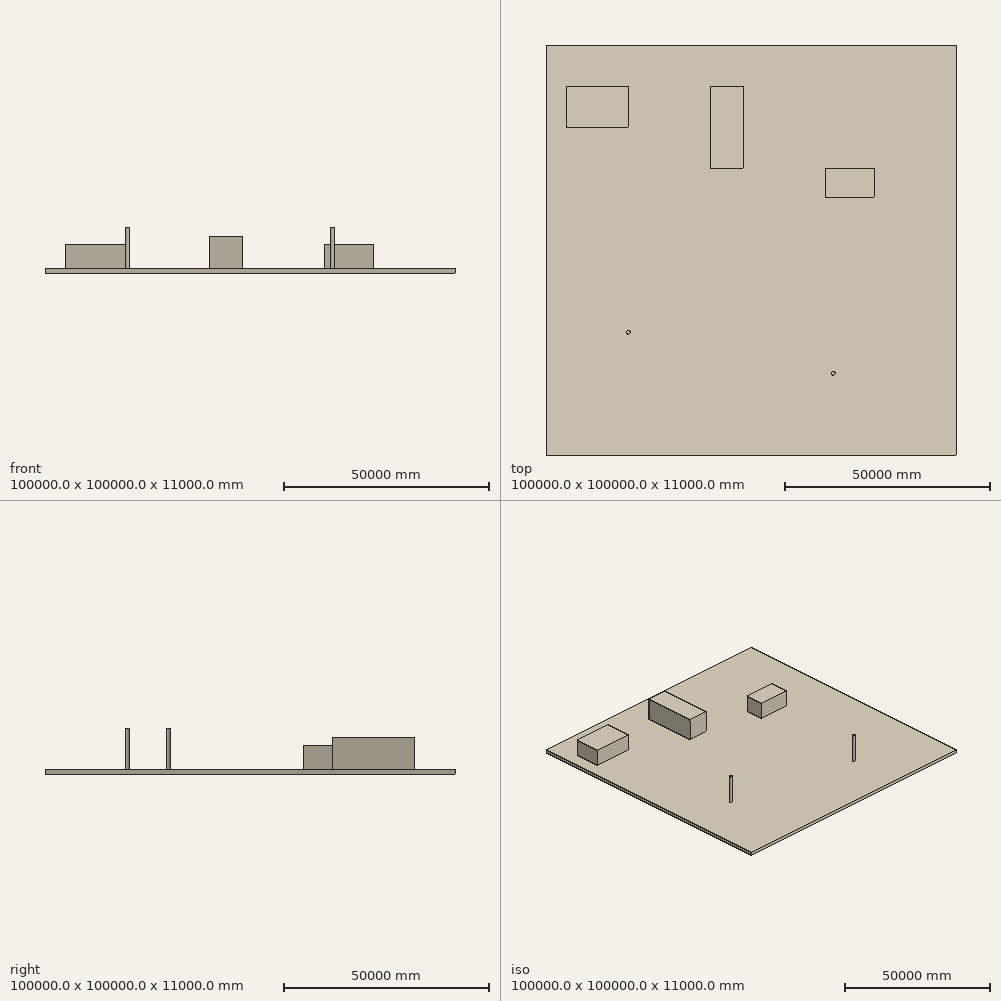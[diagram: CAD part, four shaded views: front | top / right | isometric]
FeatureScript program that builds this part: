
annotation { "Feature Type Name" : "Feature", "Feature Type Description" : "" }
export const myFeature = defineFeature(function(context is Context, id is Id, definition is map)
    precondition{}
    {
        {
            var Q0;
            Q0=qCreatedBy(makeId("Top.planeOp"),FACE);
            var sketch = newSketch(context, id + "F0", { "sketchPlane" : qUnion([Q0])});
            skLineSegment(sketch, "E0.bottom", {"start": v(-50000, 50000) * mm, "end": v(50000, 50000) * mm});
            skLineSegment(sketch, "E0.top", {"start": v(-50000, -50000) * mm, "end": v(50000, -50000) * mm});
            skLineSegment(sketch, "E0.left", {"start": v(-50000, 50000) * mm, "end": v(-50000, -50000) * mm});
            skLineSegment(sketch, "E0.right", {"start": v(50000, 50000) * mm, "end": v(50000, -50000) * mm});
            skPoint(sketch, "E0.middle", {"position": v(0, 0) * mm});
            skSolve(sketch);
        }
        {
            var Q0;
            Q0=makeQuery(id+"F0.imprint","IMPRINT",FACE,{"disambiguationData":[TD([[makeQuery(id+"F0.imprint","IMPRINT",EDGE,{"derivedFrom":sQuery(id+"F0.wireOp",EDGE,"E0.bottom")}),-1.0]])]});
            extrude(context, id + "F1", {"entities" : qUnion([Q0]), "depth" : 1000 * mm, "offsetDistance" : 25 * mm});
        }
        {
            var Q0;
            Q0=makeQuery(id+"F1.opExtrude","CAP_FACE",FACE,{"disambiguationData":[OSD([sQuery(id+"F0.wireOp",EDGE,"E0.bottom"),sQuery(id+"F0.wireOp",EDGE,"E0.top"),sQuery(id+"F0.wireOp",EDGE,"E0.left"),sQuery(id+"F0.wireOp",EDGE,"E0.right")])],"isStart":false});
            var sketch = newSketch(context, id + "F2", { "sketchPlane" : qUnion([Q0])});
            skCircle(sketch, "E1", {"center": v(20000, -30000) * mm, "radius": 500 * mm});
            skCircle(sketch, "E2", {"center": v(-30000, -20000) * mm, "radius": 500 * mm});
            skSolve(sketch);
        }
        {
            var Q0;
            Q0=makeQuery(id+"F2.imprint","IMPRINT",FACE,{"disambiguationData":[TD([[makeQuery(id+"F2.imprint","IMPRINT",EDGE,{"derivedFrom":sQuery(id+"F2.wireOp",EDGE,"E2")}),1.0]])]});
            var Q1;
            Q1=makeQuery(id+"F2.imprint","IMPRINT",FACE,{"disambiguationData":[TD([[makeQuery(id+"F2.imprint","IMPRINT",EDGE,{"derivedFrom":sQuery(id+"F2.wireOp",EDGE,"E1")}),1.0]])]});
            extrude(context, id + "F3", {"entities" : qUnion([Q0, Q1]), "operationType" : NewBodyOperationType.ADD, "depth" : 10000 * mm, "offsetDistance" : 25 * mm});
        }
        {
            var Q0;
            Q0=makeQuery(id+"F1.opExtrude","CAP_FACE",FACE,{"disambiguationData":[OSD([sQuery(id+"F0.wireOp",EDGE,"E0.bottom"),sQuery(id+"F0.wireOp",EDGE,"E0.top"),sQuery(id+"F0.wireOp",EDGE,"E0.left"),sQuery(id+"F0.wireOp",EDGE,"E0.right")])],"isStart":false});
            var sketch = newSketch(context, id + "F4", { "sketchPlane" : qUnion([Q0])});
            skLineSegment(sketch, "E3.bottom", {"start": v(-30000, 30000) * mm, "end": v(-45000, 30000) * mm});
            skLineSegment(sketch, "E3.top", {"start": v(-30000, 40000) * mm, "end": v(-45000, 40000) * mm});
            skLineSegment(sketch, "E3.left", {"start": v(-30000, 30000) * mm, "end": v(-30000, 40000) * mm});
            skLineSegment(sketch, "E3.right", {"start": v(-45000, 30000) * mm, "end": v(-45000, 40000) * mm});
            skPoint(sketch, "E3.middle", {"position": v(-37500, 35000) * mm});
            skLineSegment(sketch, "E4.bottom", {"start": v(30000, 13000) * mm, "end": v(18000, 13000) * mm});
            skLineSegment(sketch, "E4.top", {"start": v(30000, 20000) * mm, "end": v(18000, 20000) * mm});
            skLineSegment(sketch, "E4.left", {"start": v(30000, 13000) * mm, "end": v(30000, 20000) * mm});
            skLineSegment(sketch, "E4.right", {"start": v(18000, 13000) * mm, "end": v(18000, 20000) * mm});
            skPoint(sketch, "E4.middle", {"position": v(24000, 16500) * mm});
            skSolve(sketch);
        }
        {
            var Q0;
            Q0=makeQuery(id+"F4.imprint","IMPRINT",FACE,{"disambiguationData":[TD([[makeQuery(id+"F4.imprint","IMPRINT",EDGE,{"derivedFrom":sQuery(id+"F4.wireOp",EDGE,"E3.bottom")}),-1.0]])]});
            var Q1;
            Q1=makeQuery(id+"F4.imprint","IMPRINT",FACE,{"disambiguationData":[TD([[makeQuery(id+"F4.imprint","IMPRINT",EDGE,{"derivedFrom":sQuery(id+"F4.wireOp",EDGE,"E4.bottom")}),-1.0]])]});
            extrude(context, id + "F5", {"entities" : qUnion([Q0, Q1]), "depth" : 6000 * mm, "offsetDistance" : 25 * mm});
        }
        {
            var Q0;
            Q0=makeQuery(id+"F1.opExtrude","CAP_FACE",FACE,{"disambiguationData":[OSD([sQuery(id+"F0.wireOp",EDGE,"E0.bottom"),sQuery(id+"F0.wireOp",EDGE,"E0.top"),sQuery(id+"F0.wireOp",EDGE,"E0.left"),sQuery(id+"F0.wireOp",EDGE,"E0.right")])],"isStart":false});
            var sketch = newSketch(context, id + "F6", { "sketchPlane" : qUnion([Q0])});
            skLineSegment(sketch, "E5.bottom", {"start": v(-10000, 40000) * mm, "end": v(-2000, 40000) * mm});
            skLineSegment(sketch, "E5.top", {"start": v(-10000, 20000) * mm, "end": v(-2000, 20000) * mm});
            skLineSegment(sketch, "E5.left", {"start": v(-10000, 40000) * mm, "end": v(-10000, 20000) * mm});
            skLineSegment(sketch, "E5.right", {"start": v(-2000, 40000) * mm, "end": v(-2000, 20000) * mm});
            skSolve(sketch);
        }
        {
            var Q0;
            Q0=makeQuery(id+"F6.imprint","IMPRINT",FACE,{"disambiguationData":[TD([[makeQuery(id+"F6.imprint","IMPRINT",EDGE,{"derivedFrom":sQuery(id+"F6.wireOp",EDGE,"E5.bottom")}),-1.0]])]});
            extrude(context, id + "F7", {"entities" : qUnion([Q0]), "depth" : 8000 * mm, "offsetDistance" : 25 * mm});
        }
    });
